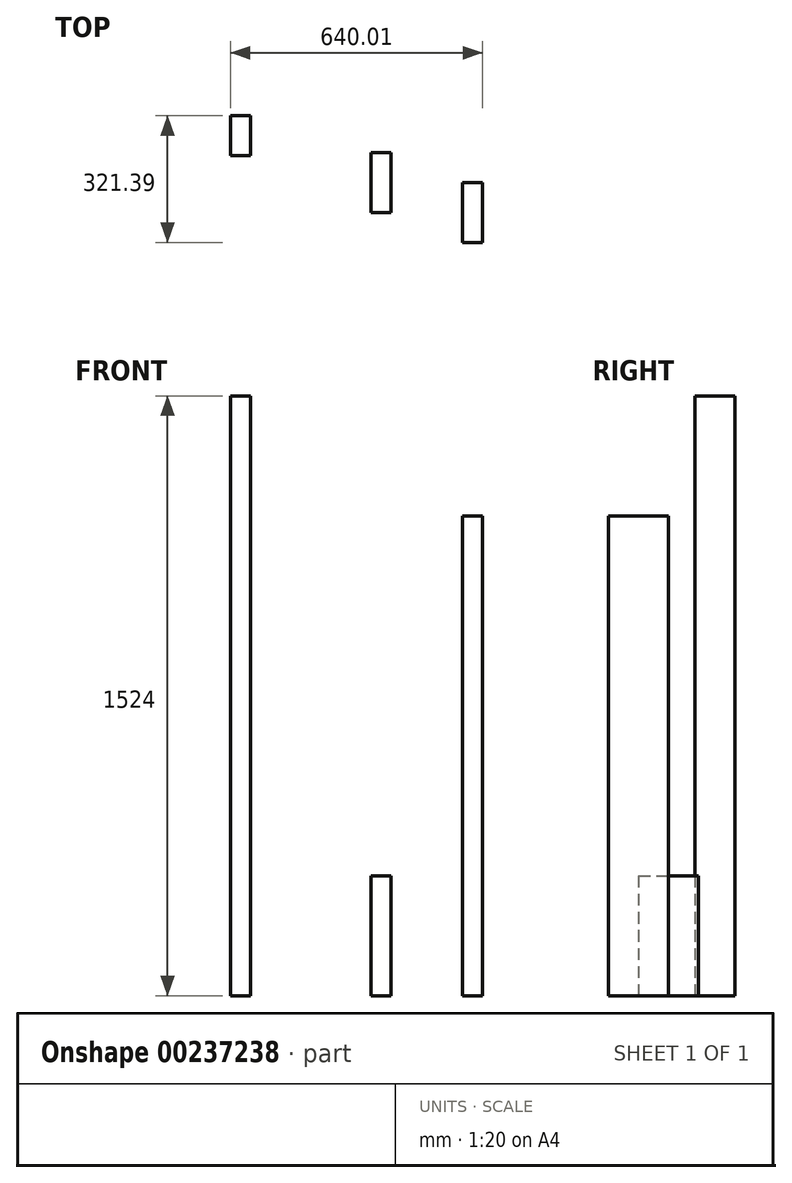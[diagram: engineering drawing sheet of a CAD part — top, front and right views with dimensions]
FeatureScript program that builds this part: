
annotation { "Feature Type Name" : "Feature", "Feature Type Description" : "" }
export const myFeature = defineFeature(function(context is Context, id is Id, definition is map)
    precondition{}
    {
        {
            var Q0;
            Q0=qCreatedBy(makeId("Top.planeOp"),FACE);
            var sketch = newSketch(context, id + "F0", { "sketchPlane" : qUnion([Q0])});
            skLineSegment(sketch, "E0.bottom", {"start": v(25.4, -76.2) * mm, "end": v(-25.4, -76.2) * mm});
            skLineSegment(sketch, "E0.top", {"start": v(25.4, 76.2) * mm, "end": v(-25.4, 76.2) * mm});
            skLineSegment(sketch, "E0.left", {"start": v(25.4, -76.2) * mm, "end": v(25.4, 76.2) * mm});
            skLineSegment(sketch, "E0.right", {"start": v(-25.4, -76.2) * mm, "end": v(-25.4, 76.2) * mm});
            skPoint(sketch, "E0.middle", {"position": v(0, 0) * mm});
            skSolve(sketch);
        }
        {
            var Q0;
            Q0=makeQuery(id+"F0.imprint","IMPRINT",FACE,{"disambiguationData":[TD([[makeQuery(id+"F0.imprint","IMPRINT",EDGE,{"derivedFrom":sQuery(id+"F0.wireOp",EDGE,"E0.bottom")}),-1.0]])]});
            extrude(context, id + "F1", {"entities" : qUnion([Q0]), "depth" : 304.8 * mm});
        }
        {
            var Q0;
            Q0=qCreatedBy(makeId("Top.planeOp"),FACE);
            var sketch = newSketch(context, id + "F2", { "sketchPlane" : qUnion([Q0])});
            skLineSegment(sketch, "E1.bottom", {"start": v(257.3, 0) * mm, "end": v(206.5, 0) * mm});
            skLineSegment(sketch, "E1.top", {"start": v(257.3, -152.4) * mm, "end": v(206.5, -152.4) * mm});
            skLineSegment(sketch, "E1.left", {"start": v(257.3, 0) * mm, "end": v(257.3, -152.4) * mm});
            skLineSegment(sketch, "E1.right", {"start": v(206.5, 0) * mm, "end": v(206.5, -152.4) * mm});
            skPoint(sketch, "E1.middle", {"position": v(231.9, -76.2) * mm});
            skSolve(sketch);
        }
        {
            var Q0;
            Q0=makeQuery(id+"F2.imprint","IMPRINT",FACE,{"disambiguationData":[TD([[makeQuery(id+"F2.imprint","IMPRINT",EDGE,{"derivedFrom":sQuery(id+"F2.wireOp",EDGE,"E1.bottom")}),1.0]])]});
            extrude(context, id + "F3", {"entities" : qUnion([Q0]), "depth" : 1219.2 * mm});
        }
        {
            var Q0;
            Q0=qCreatedBy(makeId("Top.planeOp"),FACE);
            var sketch = newSketch(context, id + "F4", { "sketchPlane" : qUnion([Q0])});
            skLineSegment(sketch, "E2.bottom", {"start": v(-382.7, 169) * mm, "end": v(-331.9, 169) * mm});
            skLineSegment(sketch, "E2.top", {"start": v(-382.7, 67.4) * mm, "end": v(-331.9, 67.4) * mm});
            skLineSegment(sketch, "E2.left", {"start": v(-382.7, 169) * mm, "end": v(-382.7, 67.4) * mm});
            skLineSegment(sketch, "E2.right", {"start": v(-331.9, 169) * mm, "end": v(-331.9, 67.4) * mm});
            skPoint(sketch, "E2.middle", {"position": v(-357.3, 118.2) * mm});
            skSolve(sketch);
        }
        {
            var Q0;
            Q0=makeQuery(id+"F4.imprint","IMPRINT",FACE,{"disambiguationData":[TD([[makeQuery(id+"F4.imprint","IMPRINT",EDGE,{"derivedFrom":sQuery(id+"F4.wireOp",EDGE,"E2.bottom")}),-1.0]])]});
            extrude(context, id + "F5", {"entities" : qUnion([Q0]), "depth" : 1524 * mm});
        }
    });
